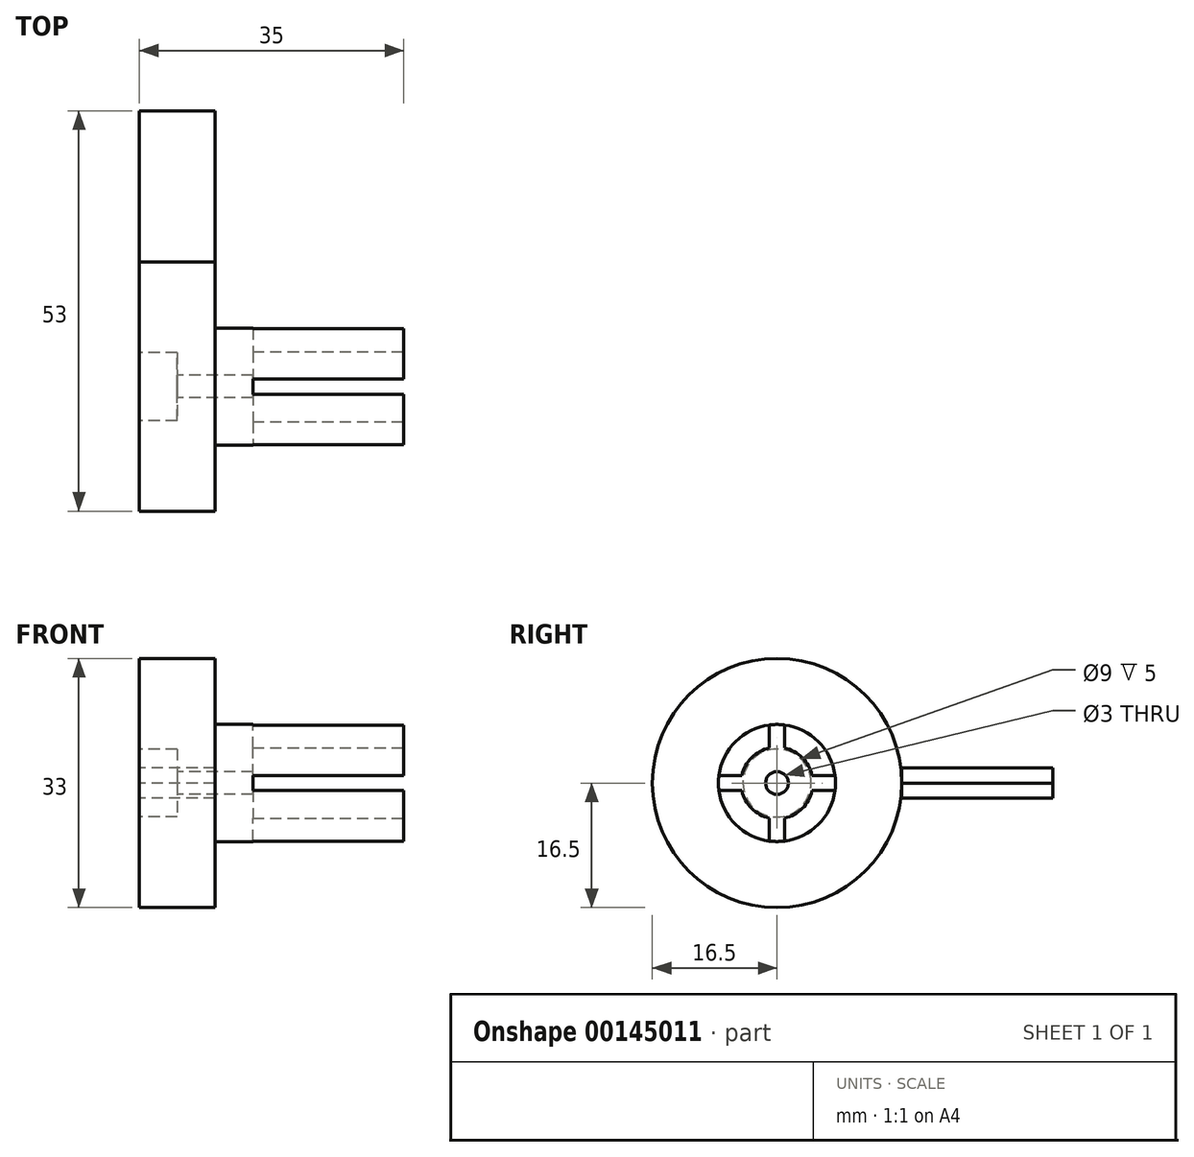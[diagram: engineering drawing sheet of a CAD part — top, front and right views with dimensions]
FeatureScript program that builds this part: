
annotation { "Feature Type Name" : "Feature", "Feature Type Description" : "" }
export const myFeature = defineFeature(function(context is Context, id is Id, definition is map)
    precondition{}
    {
        {
            var Q0;
            Q0=qCreatedBy(makeId("Top.planeOp"),FACE);
            var sketch = newSketch(context, id + "F0", { "sketchPlane" : qUnion([Q0])});
            skLineSegment(sketch, "E0.bottom", {"start": v(0, 0) * mm, "end": v(25, 0) * mm});
            skLineSegment(sketch, "E0.top", {"start": v(0, 7.75) * mm, "end": v(25, 7.75) * mm});
            skLineSegment(sketch, "E0.left", {"start": v(0, 0) * mm, "end": v(0, 7.75) * mm});
            skLineSegment(sketch, "E0.right", {"start": v(25, 0) * mm, "end": v(25, 7.75) * mm});
            skLineSegment(sketch, "E1.bottom", {"start": v(0, 0) * mm, "end": v(-10, 0) * mm});
            skLineSegment(sketch, "E1.top", {"start": v(0, 16.5) * mm, "end": v(-10, 16.5) * mm});
            skLineSegment(sketch, "E1.left", {"start": v(0, 0) * mm, "end": v(0, 16.5) * mm});
            skLineSegment(sketch, "E1.right", {"start": v(-10, 0) * mm, "end": v(-10, 16.5) * mm});
            skSolve(sketch);
        }
        {
            var Q0;
            {var subQ3=sQuery(id+"F0.wireOp",EDGE,"E1.bottom");Q0=makeQuery(id+"F0.imprint","IMPRINT",FACE,{"disambiguationData":[TD([[makeQuery(id+"F0.imprint","IMPRINT",EDGE,{"derivedFrom":subQ3}),-1.0]])]});}
            var Q1;
            {var subQ0=sQuery(id+"F0.wireOp",EDGE,"E0.bottom");Q1=makeQuery(id+"F0.imprint","IMPRINT",FACE,{"disambiguationData":[TD([[makeQuery(id+"F0.imprint","IMPRINT",EDGE,{"derivedFrom":subQ0}),1.0]])]});}
            var Q2;
            Q2=sQuery(id+"F0.wireOp",EDGE,"E0.bottom");
            revolve(context, id + "F1", {"entities" : qUnion([Q0, Q1]), "axis" : qUnion([Q2]), "revolveType" : RevolveType.FULL});
        }
        {
            var Q0;
            Q0=makeQuery(id+"F1.opRevolve","SWEPT_FACE",FACE,{"disambiguationData":[OSD([sQuery(id+"F0.wireOp",EDGE,"E0.right")])]});
            var sketch = newSketch(context, id + "F2", { "sketchPlane" : qUnion([Q0])});
            skCircle(sketch, "E2", {"center": v(0, 0) * mm, "radius": 4.75 * mm});
            skLineSegment(sketch, "E3.bottom", {"start": v(1, -10.1) * mm, "end": v(-1, -10.1) * mm});
            skLineSegment(sketch, "E3.top", {"start": v(1, 10.1) * mm, "end": v(-1, 10.1) * mm});
            skLineSegment(sketch, "E3.left", {"start": v(1, -10.1) * mm, "end": v(1, 10.1) * mm});
            skLineSegment(sketch, "E3.right", {"start": v(-1, -10.1) * mm, "end": v(-1, 10.1) * mm});
            skLineSegment(sketch, "E4.bottom", {"start": v(10.75, 1) * mm, "end": v(-10.75, 1) * mm});
            skLineSegment(sketch, "E4.top", {"start": v(10.75, -1) * mm, "end": v(-10.75, -1) * mm});
            skLineSegment(sketch, "E4.left", {"start": v(10.75, 1) * mm, "end": v(10.75, -1) * mm});
            skLineSegment(sketch, "E4.right", {"start": v(-10.75, 1) * mm, "end": v(-10.75, -1) * mm});
            skSolve(sketch);
        }
        {
            var Q0;
            {var subQ0=sQuery(id+"F2.wireOp",EDGE,"E4.bottom");var subQ1=sQuery(id+"F2.wireOp",EDGE,"E2");var subQ2=makeQuery(id+"F2.imprint","INTERSECT",VERTEX,{"disambiguationData":[OD(0.0)],"derivedFrom":[subQ1,subQ0]});Q0=makeQuery(id+"F2.imprint","IMPRINT",FACE,{"disambiguationData":[TD([[makeQuery(id+"F2.imprint","IMPRINT",EDGE,{"disambiguationData":[TD([[subQ2,1.0]])],"derivedFrom":subQ1}),-1.0]])]});}
            var Q1;
            {var subQ0=sQuery(id+"F2.wireOp",EDGE,"E4.left");Q1=makeQuery(id+"F2.imprint","IMPRINT",FACE,{"disambiguationData":[TD([[makeQuery(id+"F2.imprint","IMPRINT",EDGE,{"derivedFrom":subQ0}),-1.0]])]});}
            var Q2;
            {var subQ0=sQuery(id+"F2.wireOp",EDGE,"E4.bottom");var subQ1=sQuery(id+"F2.wireOp",EDGE,"E2");var subQ2=makeQuery(id+"F2.imprint","INTERSECT",VERTEX,{"disambiguationData":[OD(0.0)],"derivedFrom":[subQ1,subQ0]});Q2=makeQuery(id+"F2.imprint","IMPRINT",FACE,{"disambiguationData":[TD([[makeQuery(id+"F2.imprint","IMPRINT",EDGE,{"disambiguationData":[TD([[subQ2,1.0]])],"derivedFrom":subQ1}),1.0]])]});}
            var Q3;
            {var subQ0=sQuery(id+"F2.wireOp",EDGE,"E3.left");var subQ1=sQuery(id+"F2.wireOp",EDGE,"E2");var subQ2=makeQuery(id+"F2.imprint","INTERSECT",VERTEX,{"disambiguationData":[OD(0.0)],"derivedFrom":[subQ1,subQ0]});Q3=makeQuery(id+"F2.imprint","IMPRINT",FACE,{"disambiguationData":[TD([[makeQuery(id+"F2.imprint","IMPRINT",EDGE,{"disambiguationData":[TD([[subQ2,-1.0]])],"derivedFrom":subQ1}),1.0]])]});}
            var Q4;
            {var subQ0=sQuery(id+"F2.wireOp",EDGE,"E3.left");var subQ1=sQuery(id+"F2.wireOp",EDGE,"E2");var subQ2=makeQuery(id+"F2.imprint","INTERSECT",VERTEX,{"disambiguationData":[OD(0.0)],"derivedFrom":[subQ1,subQ0]});Q4=makeQuery(id+"F2.imprint","IMPRINT",FACE,{"disambiguationData":[TD([[makeQuery(id+"F2.imprint","IMPRINT",EDGE,{"disambiguationData":[TD([[subQ2,-1.0]])],"derivedFrom":subQ1}),-1.0]])]});}
            var Q5;
            {var subQ0=sQuery(id+"F2.wireOp",EDGE,"E3.top");Q5=makeQuery(id+"F2.imprint","IMPRINT",FACE,{"disambiguationData":[TD([[makeQuery(id+"F2.imprint","IMPRINT",EDGE,{"derivedFrom":subQ0}),1.0]])]});}
            var Q6;
            {var subQ0=sQuery(id+"F2.wireOp",EDGE,"E4.top");var subQ1=sQuery(id+"F2.wireOp",EDGE,"E3.left");var subQ2=makeQuery(id+"F2.imprint","INTERSECT",VERTEX,{"derivedFrom":[subQ1,subQ0]});Q6=makeQuery(id+"F2.imprint","IMPRINT",FACE,{"disambiguationData":[TD([[makeQuery(id+"F2.imprint","IMPRINT",EDGE,{"disambiguationData":[TD([[subQ2,-1.0]])],"derivedFrom":subQ1}),1.0]])]});}
            var Q7;
            {var subQ0=sQuery(id+"F2.wireOp",EDGE,"E3.right");var subQ1=sQuery(id+"F2.wireOp",EDGE,"E2");var subQ2=makeQuery(id+"F2.imprint","INTERSECT",VERTEX,{"disambiguationData":[OD(1.0)],"derivedFrom":[subQ1,subQ0]});Q7=makeQuery(id+"F2.imprint","IMPRINT",FACE,{"disambiguationData":[TD([[makeQuery(id+"F2.imprint","IMPRINT",EDGE,{"disambiguationData":[TD([[subQ2,-1.0]])],"derivedFrom":subQ1}),1.0]])]});}
            var Q8;
            {var subQ0=sQuery(id+"F2.wireOp",EDGE,"E3.right");var subQ1=sQuery(id+"F2.wireOp",EDGE,"E2");var subQ2=makeQuery(id+"F2.imprint","INTERSECT",VERTEX,{"disambiguationData":[OD(1.0)],"derivedFrom":[subQ1,subQ0]});Q8=makeQuery(id+"F2.imprint","IMPRINT",FACE,{"disambiguationData":[TD([[makeQuery(id+"F2.imprint","IMPRINT",EDGE,{"disambiguationData":[TD([[subQ2,-1.0]])],"derivedFrom":subQ1}),-1.0]])]});}
            var Q9;
            {var subQ0=sQuery(id+"F2.wireOp",EDGE,"E3.bottom");Q9=makeQuery(id+"F2.imprint","IMPRINT",FACE,{"disambiguationData":[TD([[makeQuery(id+"F2.imprint","IMPRINT",EDGE,{"derivedFrom":subQ0}),-1.0]])]});}
            var Q10;
            {var subQ0=sQuery(id+"F2.wireOp",EDGE,"E4.bottom");var subQ1=sQuery(id+"F2.wireOp",EDGE,"E2");var subQ2=makeQuery(id+"F2.imprint","INTERSECT",VERTEX,{"disambiguationData":[OD(1.0)],"derivedFrom":[subQ1,subQ0]});Q10=makeQuery(id+"F2.imprint","IMPRINT",FACE,{"disambiguationData":[TD([[makeQuery(id+"F2.imprint","IMPRINT",EDGE,{"disambiguationData":[TD([[subQ2,-1.0]])],"derivedFrom":subQ1}),1.0]])]});}
            var Q11;
            {var subQ0=sQuery(id+"F2.wireOp",EDGE,"E4.bottom");var subQ1=sQuery(id+"F2.wireOp",EDGE,"E2");var subQ2=makeQuery(id+"F2.imprint","INTERSECT",VERTEX,{"disambiguationData":[OD(1.0)],"derivedFrom":[subQ1,subQ0]});Q11=makeQuery(id+"F2.imprint","IMPRINT",FACE,{"disambiguationData":[TD([[makeQuery(id+"F2.imprint","IMPRINT",EDGE,{"disambiguationData":[TD([[subQ2,-1.0]])],"derivedFrom":subQ1}),-1.0]])]});}
            var Q12;
            {var subQ0=sQuery(id+"F2.wireOp",EDGE,"E4.right");Q12=makeQuery(id+"F2.imprint","IMPRINT",FACE,{"disambiguationData":[TD([[makeQuery(id+"F2.imprint","IMPRINT",EDGE,{"derivedFrom":subQ0}),1.0]])]});}
            var Q13;
            {var subQ0=sQuery(id+"F2.wireOp",EDGE,"E3.right");var subQ1=sQuery(id+"F2.wireOp",EDGE,"E2");var subQ2=makeQuery(id+"F2.imprint","INTERSECT",VERTEX,{"disambiguationData":[OD(0.0)],"derivedFrom":[subQ1,subQ0]});Q13=makeQuery(id+"F2.imprint","IMPRINT",FACE,{"disambiguationData":[TD([[makeQuery(id+"F2.imprint","IMPRINT",EDGE,{"disambiguationData":[TD([[subQ2,-1.0]])],"derivedFrom":subQ1}),1.0]])]});}
            var Q14;
            {var subQ0=sQuery(id+"F2.wireOp",EDGE,"E4.top");var subQ1=sQuery(id+"F2.wireOp",EDGE,"E2");var subQ2=makeQuery(id+"F2.imprint","INTERSECT",VERTEX,{"disambiguationData":[OD(0.0)],"derivedFrom":[subQ1,subQ0]});Q14=makeQuery(id+"F2.imprint","IMPRINT",FACE,{"disambiguationData":[TD([[makeQuery(id+"F2.imprint","IMPRINT",EDGE,{"disambiguationData":[TD([[subQ2,-1.0]])],"derivedFrom":subQ1}),1.0]])]});}
            var Q15;
            {var subQ0=sQuery(id+"F2.wireOp",EDGE,"E3.left");var subQ1=sQuery(id+"F2.wireOp",EDGE,"E2");var subQ2=makeQuery(id+"F2.imprint","INTERSECT",VERTEX,{"disambiguationData":[OD(1.0)],"derivedFrom":[subQ1,subQ0]});Q15=makeQuery(id+"F2.imprint","IMPRINT",FACE,{"disambiguationData":[TD([[makeQuery(id+"F2.imprint","IMPRINT",EDGE,{"disambiguationData":[TD([[subQ2,-1.0]])],"derivedFrom":subQ1}),1.0]])]});}
            var Q16;
            {var subQ0=sQuery(id+"F2.wireOp",EDGE,"E3.left");var subQ1=sQuery(id+"F2.wireOp",EDGE,"E2");var subQ2=makeQuery(id+"F2.imprint","INTERSECT",VERTEX,{"disambiguationData":[OD(0.0)],"derivedFrom":[subQ1,subQ0]});Q16=makeQuery(id+"F2.imprint","IMPRINT",FACE,{"disambiguationData":[TD([[makeQuery(id+"F2.imprint","IMPRINT",EDGE,{"disambiguationData":[TD([[subQ2,1.0]])],"derivedFrom":subQ1}),1.0]])]});}
            extrude(context, id + "F3", {"entities" : qUnion([Q0, Q1, Q2, Q3, Q4, Q5, Q6, Q7, Q8, Q9, Q10, Q11, Q12, Q13, Q14, Q15, Q16]), "operationType" : NewBodyOperationType.REMOVE, "oppositeDirection" : true, "depth" : 20 * mm});
        }
        {
            var Q0;
            Q0=makeQuery(id+"F1.opRevolve","SWEPT_FACE",FACE,{"disambiguationData":[OSD([sQuery(id+"F0.wireOp",EDGE,"E1.right")])]});
            var sketch = newSketch(context, id + "F4", { "sketchPlane" : qUnion([Q0])});
            skCircle(sketch, "E5", {"center": v(0, 0) * mm, "radius": 4.5 * mm});
            skCircle(sketch, "E6", {"center": v(0, 0) * mm, "radius": 1.5 * mm});
            skSolve(sketch);
        }
        {
            var Q0;
            Q0 = qSketchRegion(id + "F4", true);
            extrude(context, id + "F5", {"entities" : qUnion([Q0]), "operationType" : NewBodyOperationType.REMOVE, "oppositeDirection" : true, "depth" : 5 * mm});
        }
        {
            var Q0;
            Q0=makeQuery(id+"F5.boolean.opBoolean","SPLIT",FACE,{"disambiguationData":[TD([makeQuery(id+"F5.opExtrude","SWEPT_FACE",FACE,{"disambiguationData":[OSD([sQuery(id+"F4.wireOp",EDGE,"E6")])]})])],"derivedFrom":makeQuery(id+"F1.opRevolve","SWEPT_FACE",FACE,{"disambiguationData":[OSD([sQuery(id+"F0.wireOp",EDGE,"E1.right")])]})});
            extrude(context, id + "F6", {"entities" : qUnion([Q0]), "operationType" : NewBodyOperationType.REMOVE, "oppositeDirection" : true, "depth" : 25 * mm});
        }
        {
            var Q0;
            Q0=qCreatedBy(makeId("Top.planeOp"),FACE);
            var sketch = newSketch(context, id + "F7", { "sketchPlane" : qUnion([Q0])});
            skLineSegment(sketch, "E7.bottom", {"start": v(0, 16.5) * mm, "end": v(-10, 16.5) * mm});
            skLineSegment(sketch, "E7.top", {"start": v(0, 36.5) * mm, "end": v(-10, 36.5) * mm});
            skLineSegment(sketch, "E7.left", {"start": v(0, 16.5) * mm, "end": v(0, 36.5) * mm});
            skLineSegment(sketch, "E7.right", {"start": v(-10, 16.5) * mm, "end": v(-10, 36.5) * mm});
            skSolve(sketch);
        }
        {
            var Q0;
            Q0 = qSketchRegion(id + "F7", true);
            extrude(context, id + "F8", {"entities" : qUnion([Q0]), "depth" : 2 * mm});
        }
        {
            var Q0;
            Q0=makeQuery(id+"F7.imprint","IMPRINT",FACE,{"disambiguationData":[TD([[makeQuery(id+"F7.imprint","IMPRINT",EDGE,{"derivedFrom":sQuery(id+"F7.wireOp",EDGE,"KncD7h4H-aaDO-UcPn-uRx5-9DAQhZDxX1kB.top")}),1.0]])]});
            var Q1;
            Q1=makeQuery(id+"F7.imprint","IMPRINT",FACE,{"disambiguationData":[TD([[makeQuery(id+"F7.imprint","IMPRINT",EDGE,{"derivedFrom":sQuery(id+"F7.wireOp",EDGE,"E7.bottom")}),-1.0]])]});
            var Q2;
            Q2 = qConstructionFilter(qBodyType(qCreatedBy(id + "F7" ,EDGE), BodyType.WIRE), ConstructionObject.NO);
            extrude(context, id + "F9", {"entities" : qUnion([Q0, Q1]), "surfaceEntities" : qUnion([Q2]), "oppositeDirection" : true, "depth" : 2 * mm});
        }
    });
